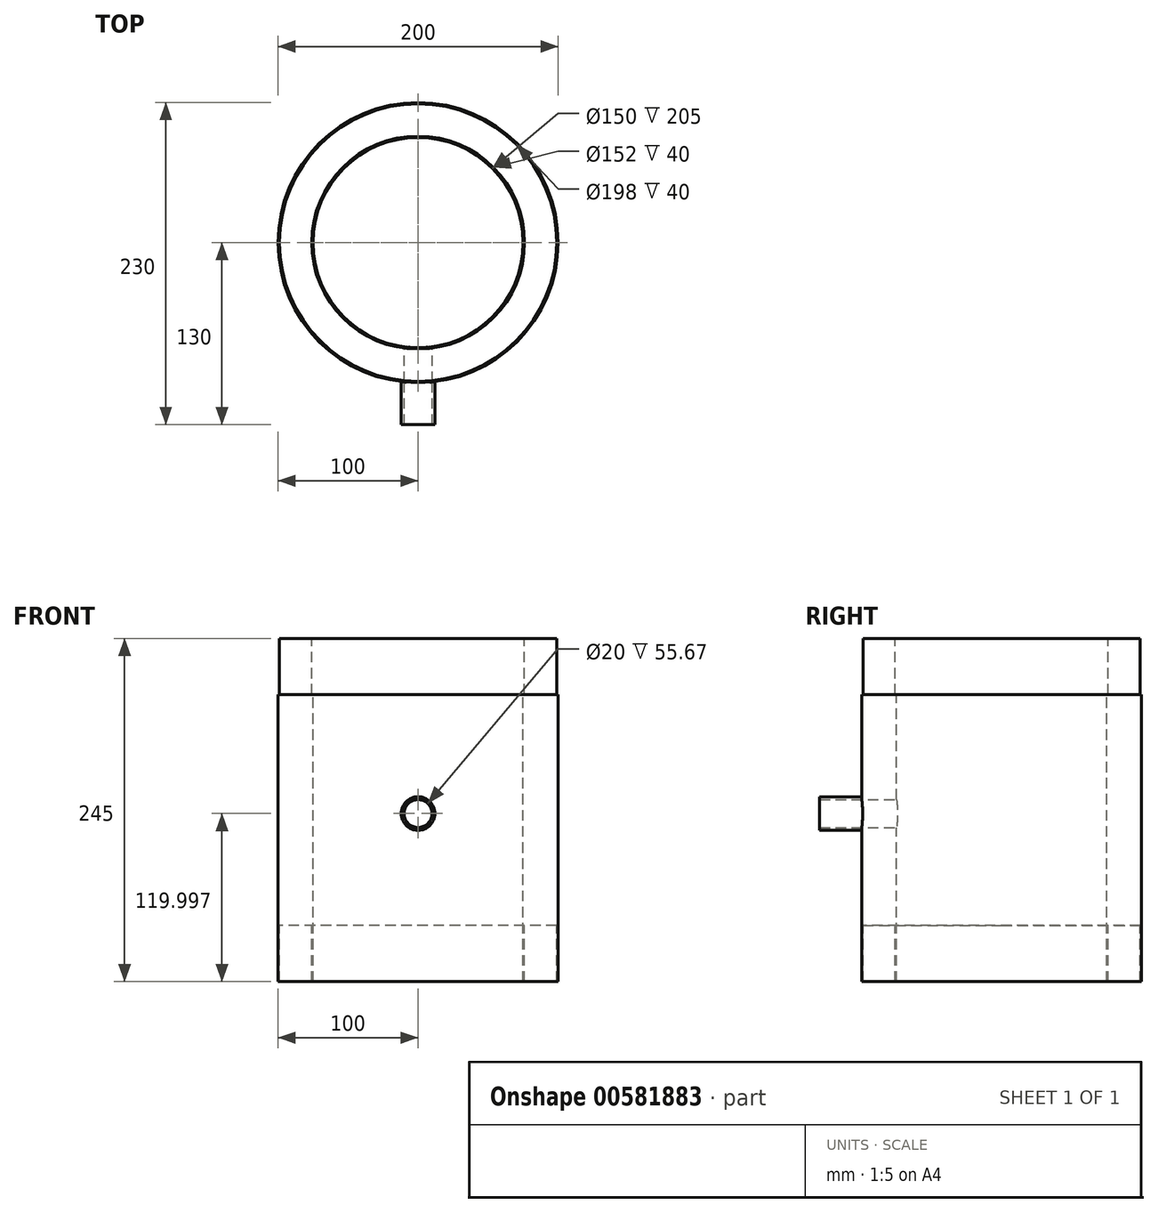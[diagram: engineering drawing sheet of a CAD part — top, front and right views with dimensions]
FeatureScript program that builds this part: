
annotation { "Feature Type Name" : "Feature", "Feature Type Description" : "" }
export const myFeature = defineFeature(function(context is Context, id is Id, definition is map)
    precondition{}
    {
        {
            var Q0;
            Q0=qCreatedBy(makeId("Front.planeOp"),FACE);
            var sketch = newSketch(context, id + "F0", { "sketchPlane" : qUnion([Q0])});
            skLineSegment(sketch, "E0", {"start": v(0, 74.87) * mm, "end": v(0, -73.71) * mm, "construction": true});
            skLineSegment(sketch, "E1", {"start": v(0, 374.84) * mm, "end": v(0, -528.94) * mm, "construction": true});
            skLineSegment(sketch, "E2", {"start": v(-75, -489.75) * mm, "end": v(-75, -284.75) * mm});
            skLineSegment(sketch, "E3", {"start": v(-75, -284.75) * mm, "end": v(-76, -284.75) * mm});
            skLineSegment(sketch, "E4", {"start": v(-76, -284.75) * mm, "end": v(-76, -244.75) * mm});
            skLineSegment(sketch, "E5", {"start": v(-76, -244.75) * mm, "end": v(-99, -244.75) * mm});
            skLineSegment(sketch, "E6", {"start": v(-99, -244.75) * mm, "end": v(-99, -284.75) * mm});
            skLineSegment(sketch, "E7", {"start": v(-99, -284.75) * mm, "end": v(-100, -284.75) * mm});
            skLineSegment(sketch, "E8", {"start": v(-100, -284.75) * mm, "end": v(-100, -489.75) * mm});
            skLineSegment(sketch, "E9", {"start": v(-100, -489.75) * mm, "end": v(-99, -489.75) * mm});
            skLineSegment(sketch, "E10", {"start": v(-99, -489.75) * mm, "end": v(-99, -449.75) * mm});
            skLineSegment(sketch, "E11", {"start": v(-99, -449.75) * mm, "end": v(-76, -449.75) * mm});
            skLineSegment(sketch, "E12", {"start": v(-76, -449.75) * mm, "end": v(-76, -489.75) * mm});
            skLineSegment(sketch, "E13", {"start": v(-76, -489.75) * mm, "end": v(-75, -489.75) * mm});
            skSolve(sketch);
        }
        {
            var Q0;
            Q0=qSketchRegion(id+"F0",true);
            var Q1;
            Q1=sQuery(id+"F0.wireOp",EDGE,"E1");
            revolve(context, id + "F1", {"entities" : qUnion([Q0]), "axis" : qUnion([Q1]), "revolveType" : RevolveType.FULL});
        }
        {
            var Q0;
            Q0=qCreatedBy(makeId("Front.planeOp"),FACE);
            var sketch = newSketch(context, id + "F2", { "sketchPlane" : qUnion([Q0])});
            skLineSegment(sketch, "E14", {"start": v(0, 0) * mm, "end": v(0, -739.5) * mm, "construction": true});
            skCircle(sketch, "E15", {"center": v(0, -369.75) * mm, "radius": 10 * mm});
            skLineSegment(sketch, "E16.0", {"start": v(-99, -244.75) * mm, "end": v(99, -244.75) * mm, "construction": true});
            skSolve(sketch);
        }
        {
            var Q0;
            Q0=qSketchRegion(id+"F2",true);
            extrude(context, id + "F3", {"entities" : qUnion([Q0]), "operationType" : NewBodyOperationType.REMOVE, "depth" : 661 * mm});
        }
        {
            var Q0;
            Q0=qCreatedBy(makeId("Front.planeOp"),FACE);
            cPlane(context, id + "F4", {"entities" : qUnion([Q0]), "cplaneType" : CPlaneType.OFFSET, "offset" : 80 * mm, "width" : 150 * mm, "height" : 150 * mm});
        }
        {
            var Q0;
            Q0=qCreatedBy(id+"F4.planeOp",FACE);
            var sketch = newSketch(context, id + "F5", { "sketchPlane" : qUnion([Q0])});
            skLineSegment(sketch, "E17", {"start": v(0, 0) * mm, "end": v(0, -620.93) * mm, "construction": true});
            skLineSegment(sketch, "E18.0", {"start": v(-99, -244.75) * mm, "end": v(99, -244.75) * mm, "construction": true});
            skCircle(sketch, "E19.0", {"center": v(0, -369.75) * mm, "radius": 10 * mm});
            skCircle(sketch, "E20", {"center": v(0, -369.75) * mm, "radius": 12 * mm});
            skSolve(sketch);
        }
        {
            var Q0;
            Q0=qSketchRegion(id+"F5",true);
            extrude(context, id + "F6", {"entities" : qUnion([Q0]), "operationType" : NewBodyOperationType.ADD, "depth" : 50 * mm, "offsetDistance" : 25 * mm});
        }
    });
